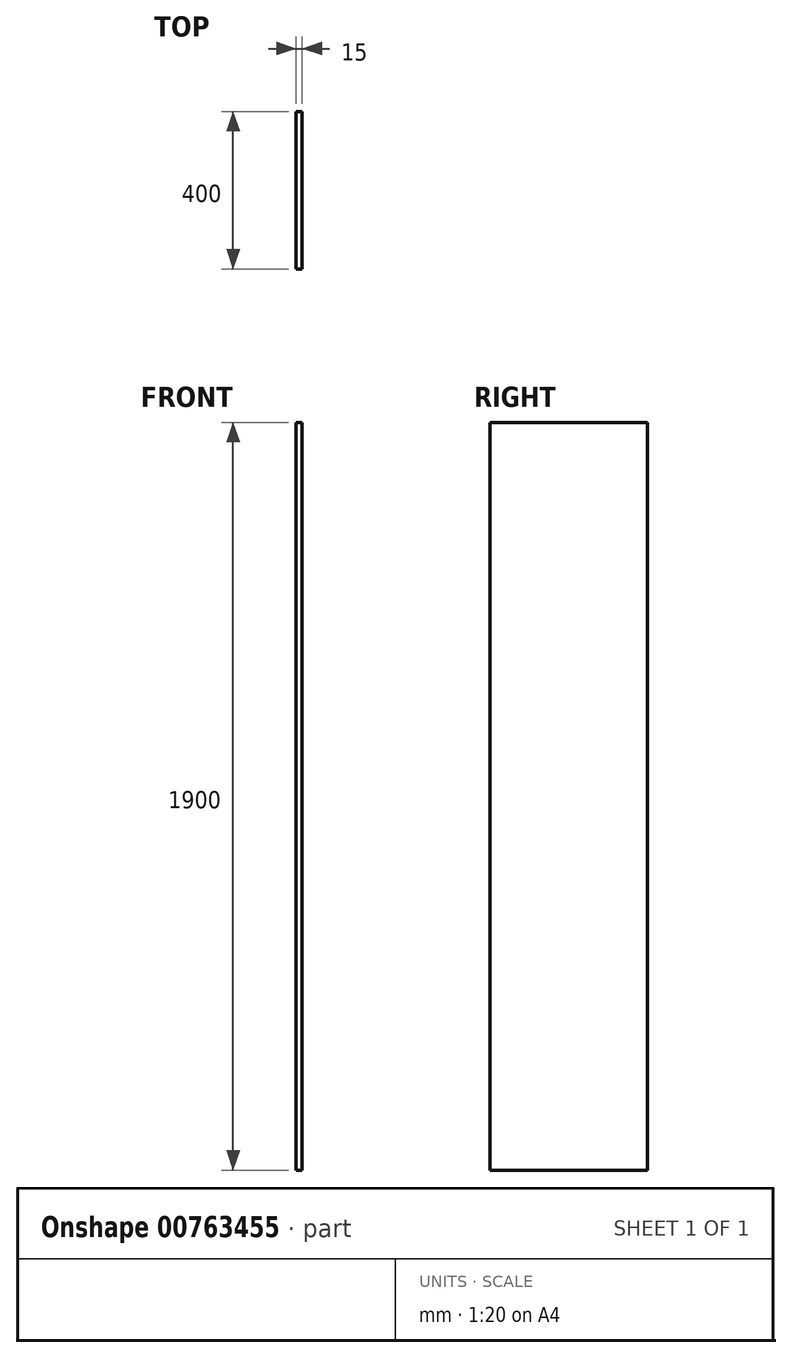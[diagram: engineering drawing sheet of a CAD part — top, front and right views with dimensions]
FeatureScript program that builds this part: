
annotation { "Feature Type Name" : "Feature", "Feature Type Description" : "" }
export const myFeature = defineFeature(function(context is Context, id is Id, definition is map)
    precondition{}
    {
        {
            var Q0;
            Q0=qCreatedBy(makeId("Right.planeOp"), FACE);
            var sketch = newSketch(context, id + "F0", { "sketchPlane" : qUnion([Q0])});
            skLineSegment(sketch, "E0.bottom", {"start": v(0, 0) * mm, "end": v(400, 0) * mm});
            skLineSegment(sketch, "E0.top", {"start": v(0, 1900) * mm, "end": v(400, 1900) * mm});
            skLineSegment(sketch, "E0.left", {"start": v(0, 0) * mm, "end": v(0, 1900) * mm});
            skLineSegment(sketch, "E0.right", {"start": v(400, 0) * mm, "end": v(400, 1900) * mm});
            skSolve(sketch);
        }
        {
            var Q0;
            Q0 = qSketchRegion(id + "F0", true);
            extrude(context, id + "F1", {"entities" : qUnion([Q0]), "domain" : OperationDomain.MODEL, "flatOperationType" : FlatOperationType.REMOVE, "depth" : 15 * mm, "offsetDistance" : 25.4 * mm});
        }
    });
